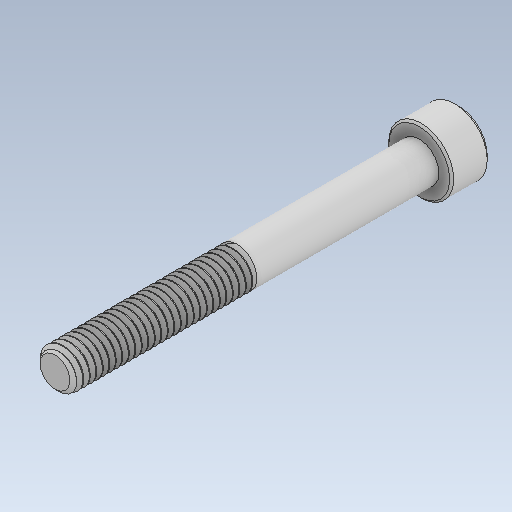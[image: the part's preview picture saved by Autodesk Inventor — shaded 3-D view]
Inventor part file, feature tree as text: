
AUTODESK INVENTOR PART (.ipt)
format: ipt  version: 2020 (Build 240168000, 168)  size: 706,560 bytes
history: native  units: in
note: dims shown in document units (in); Inventor stores cm internally (conversion verified against a paired STEP export)
features: chamfer x1
ambient origin geometry x8: Origin, YZ Plane, XZ Plane, XY Plane, X Axis, Y Axis, Z Axis, Center Point
bodies: Solid1 (feature_tree)
feature tree (1):
  chamfer  "Chamfer2"  [1 undecoded]
note: 1 required parameter value undecoded (feature->parameter linkage not recoverable at this tier; creation-order binding heuristic only, values carry confidence <= 0.55)
